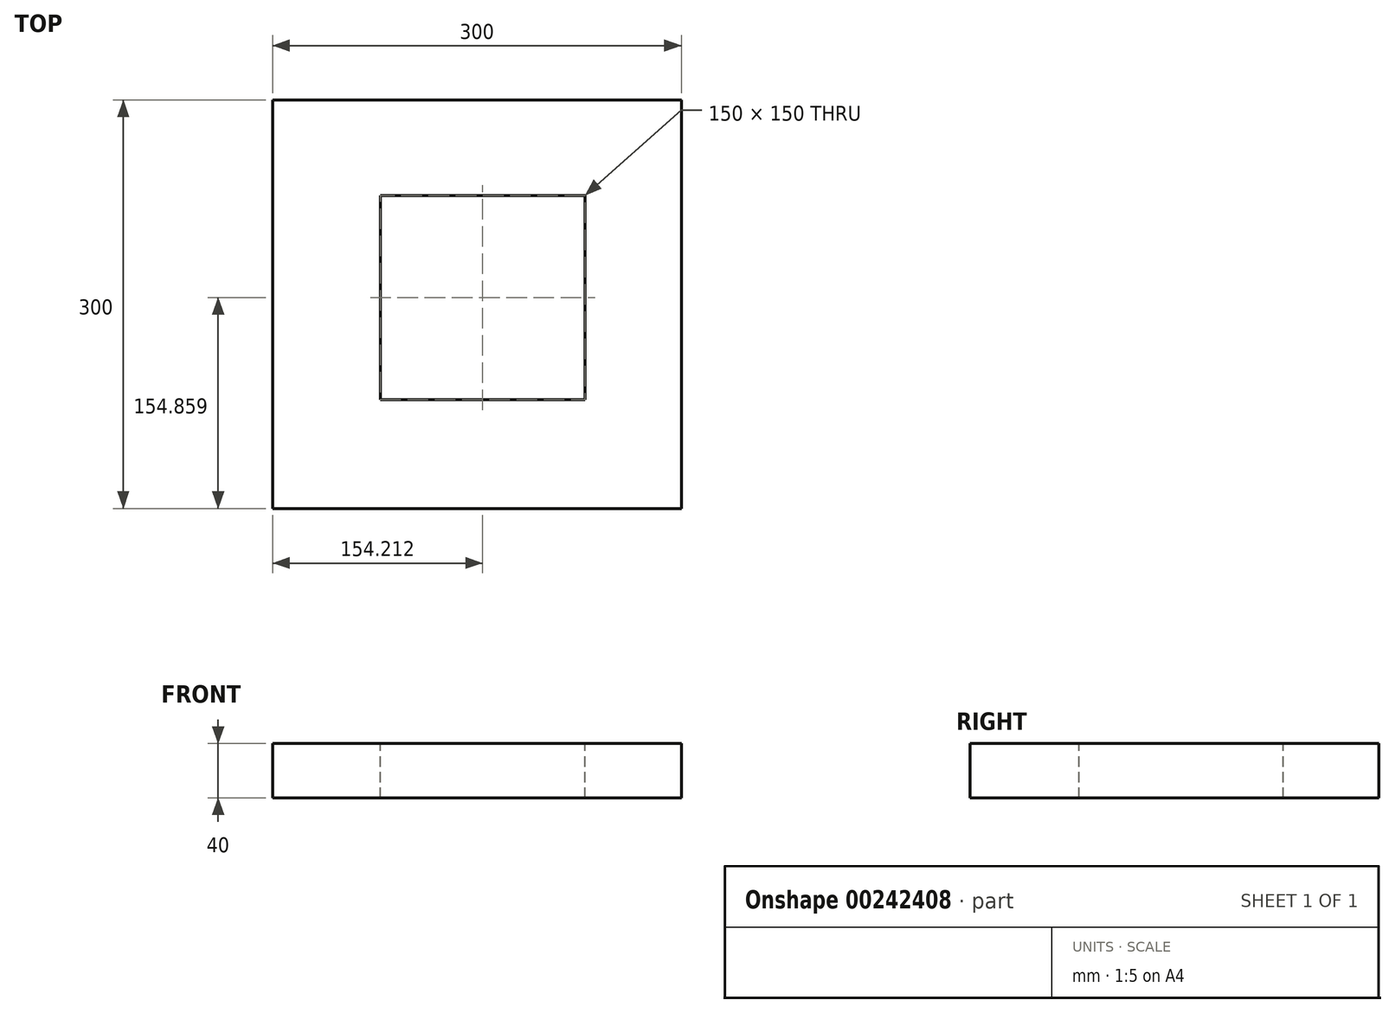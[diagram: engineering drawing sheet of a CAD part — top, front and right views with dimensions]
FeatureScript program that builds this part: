
annotation { "Feature Type Name" : "Feature", "Feature Type Description" : "" }
export const myFeature = defineFeature(function(context is Context, id is Id, definition is map)
    precondition{}
    {
        {
            var Q0;
            Q0=qCreatedBy(makeId("Top.planeOp"),FACE);
            var sketch = newSketch(context, id + "F0", { "sketchPlane" : qUnion([Q0])});
            skLineSegment(sketch, "E0.bottom", {"start": v(-154.05, -154) * mm, "end": v(145.95, -154) * mm});
            skLineSegment(sketch, "E0.top", {"start": v(-154.05, 146) * mm, "end": v(145.95, 146) * mm});
            skLineSegment(sketch, "E0.left", {"start": v(-154.05, -154) * mm, "end": v(-154.05, 146) * mm});
            skLineSegment(sketch, "E0.right", {"start": v(145.95, -154) * mm, "end": v(145.95, 146) * mm});
            skSolve(sketch);
        }
        {
            var Q0;
            Q0=makeQuery(id+"F0.imprint","IMPRINT",FACE,{"disambiguationData":[TD([[makeQuery(id+"F0.imprint","IMPRINT",EDGE,{"derivedFrom":sQuery(id+"F0.wireOp",EDGE,"E0.bottom")}),1.0]])]});
            extrude(context, id + "F1", {"entities" : qUnion([Q0]), "endBound" : BoundingType.SYMMETRIC, "depth" : 40 * mm});
        }
        {
            var Q0;
            Q0=makeQuery(id+"F1.opExtrude","CAP_FACE",FACE,{"disambiguationData":[OSD([sQuery(id+"F0.wireOp",EDGE,"E0.bottom"),sQuery(id+"F0.wireOp",EDGE,"E0.top"),sQuery(id+"F0.wireOp",EDGE,"E0.left"),sQuery(id+"F0.wireOp",EDGE,"E0.right")])],"isStart":false});
            var sketch = newSketch(context, id + "F2", { "sketchPlane" : qUnion([Q0])});
            skLineSegment(sketch, "E1.bottom", {"start": v(-74.84, 75.86) * mm, "end": v(75.16, 75.86) * mm});
            skLineSegment(sketch, "E1.top", {"start": v(-74.84, -74.14) * mm, "end": v(75.16, -74.14) * mm});
            skLineSegment(sketch, "E1.left", {"start": v(-74.84, 75.86) * mm, "end": v(-74.84, -74.14) * mm});
            skLineSegment(sketch, "E1.right", {"start": v(75.16, 75.86) * mm, "end": v(75.16, -74.14) * mm});
            skSolve(sketch);
        }
        {
            var Q0;
            Q0=makeQuery(id+"F2.imprint","IMPRINT",FACE,{"disambiguationData":[TD([[makeQuery(id+"F2.imprint","IMPRINT",EDGE,{"derivedFrom":sQuery(id+"F2.wireOp",EDGE,"E1.bottom")}),-1.0]])]});
            extrude(context, id + "F3", {"entities" : qUnion([Q0]), "operationType" : NewBodyOperationType.REMOVE, "oppositeDirection" : true, "depth" : 50 * mm});
        }
    });
